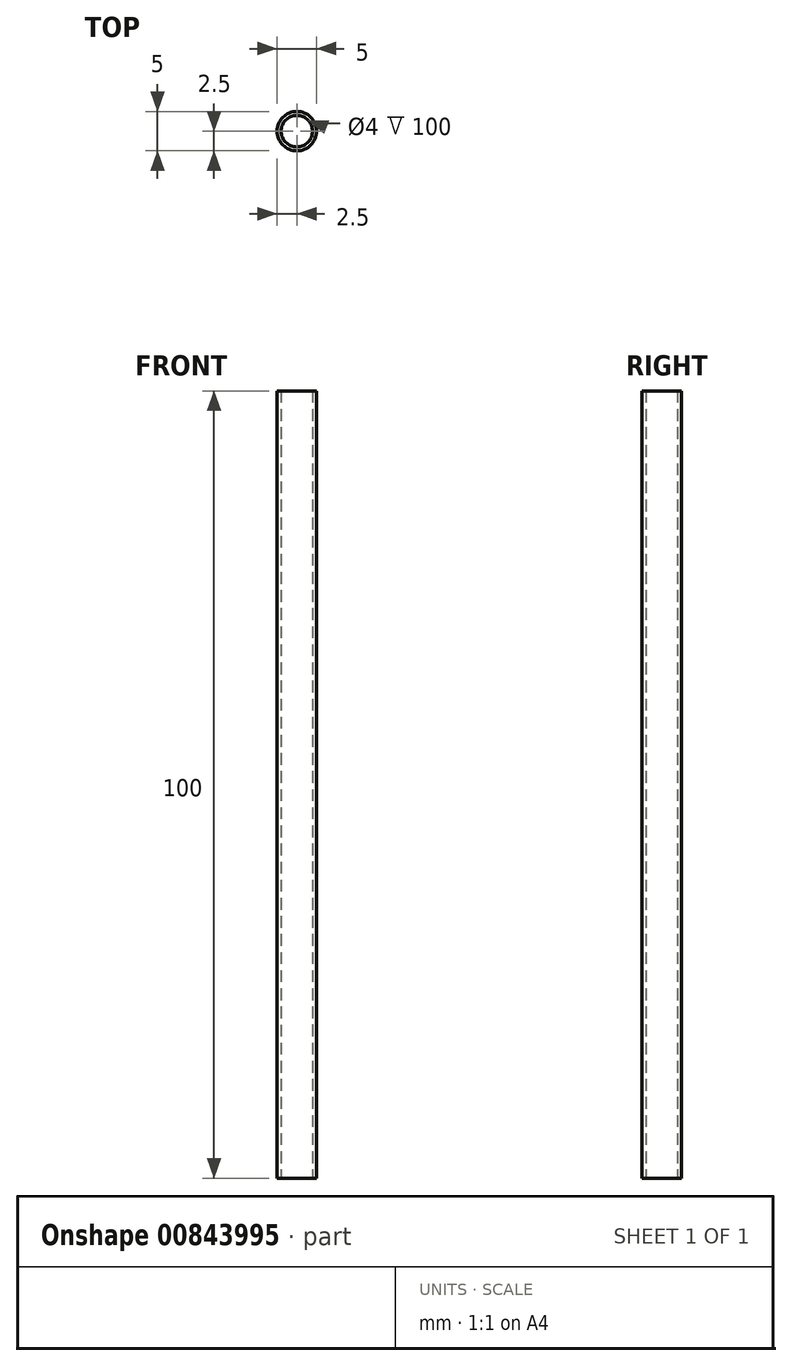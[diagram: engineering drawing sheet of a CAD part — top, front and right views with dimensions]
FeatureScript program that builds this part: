
annotation { "Feature Type Name" : "Feature", "Feature Type Description" : "" }
export const myFeature = defineFeature(function(context is Context, id is Id, definition is map)
    precondition{}
    {
        {
            var Q0;
            Q0=qCreatedBy(makeId("Top.planeOp"),FACE);
            var sketch = newSketch(context, id + "F0", { "sketchPlane" : qUnion([Q0])});
            skCircle(sketch, "E0", {"center": v(0, 0) * mm, "radius": 2.5 * mm});
            skSolve(sketch);
        }
        {
            var Q0;
            Q0=makeQuery(id+"F0.imprint","IMPRINT",FACE,{"disambiguationData":[TD([[makeQuery(id+"F0.imprint","IMPRINT",EDGE,{"derivedFrom":sQuery(id+"F0.wireOp",EDGE,"E0")}),1.0]])]});
            extrude(context, id + "F1", {"entities" : qUnion([Q0]), "depth" : 100 * mm, "offsetDistance" : 25 * mm});
        }
        {
            var Q0;
            Q0=makeQuery(id+"F1.opExtrude","CAP_FACE",FACE,{"disambiguationData":[OSD([sQuery(id+"F0.wireOp",EDGE,"E0")])],"isStart":true});
            var sketch = newSketch(context, id + "F2", { "sketchPlane" : qUnion([Q0])});
            skCircle(sketch, "E1", {"center": v(0, 0) * mm, "radius": 2 * mm});
            skSolve(sketch);
        }
        {
            var Q0;
            Q0 = qSketchRegion(id + "F2", true);
            extrude(context, id + "F3", {"entities" : qUnion([Q0]), "operationType" : NewBodyOperationType.REMOVE, "oppositeDirection" : true, "depth" : 105 * mm, "offsetDistance" : 25 * mm});
        }
    });
